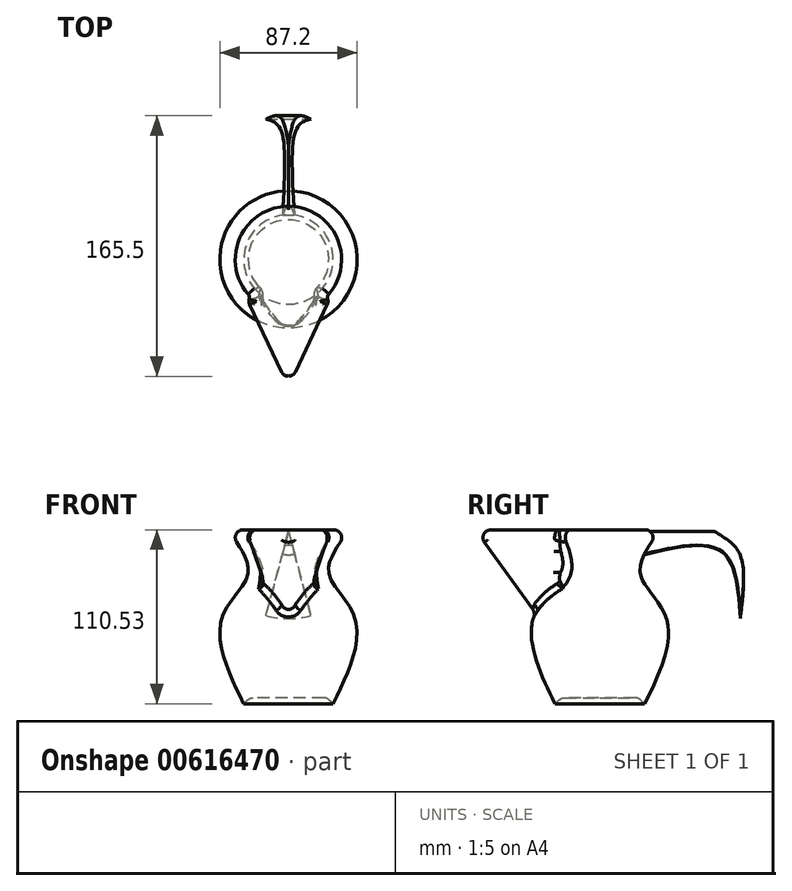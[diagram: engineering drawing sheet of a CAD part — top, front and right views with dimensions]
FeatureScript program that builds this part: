
annotation { "Feature Type Name" : "Feature", "Feature Type Description" : "" }
export const myFeature = defineFeature(function(context is Context, id is Id, definition is map)
    precondition{}
    {
        {
            var Q0;
            Q0=qCreatedBy(makeId("Front.planeOp"),FACE);
            var sketch = newSketch(context, id + "F0", { "sketchPlane" : qUnion([Q0])});
            skLineSegment(sketch, "E0", {"start": v(0, 56.43) * mm, "end": v(0, -56.06) * mm});
            skLineSegment(sketch, "E1", {"start": v(0, 56.43) * mm, "end": v(-38.4, 56.43) * mm});
            skFitSpline(sketch, "E2", {"points": [v(-38.4, 56.43) * mm, v(-26.17, 26.6) * mm, v(-42.35, 0) * mm, v(-27.43, -55.98) * mm], "startDerivative": vector(98.97, -136.85) * mm, "endDerivative": vector(82.52, -160.43) * mm});
            skLineSegment(sketch, "E3", {"start": v(0, -56.06) * mm, "end": v(-27.43, -55.98) * mm});
            skSolve(sketch);
        }
        {
            var Q0;
            Q0=makeQuery(id+"F0.imprint","IMPRINT",FACE,{"disambiguationData":[TD([[makeQuery(id+"F0.imprint","IMPRINT",EDGE,{"derivedFrom":sQuery(id+"F0.wireOp",EDGE,"E0")}),-1.0]])]});
            var Q1;
            Q1=sQuery(id+"F0.wireOp",EDGE,"E0");
            revolve(context, id + "F1", {"entities" : qUnion([Q0]), "axis" : qUnion([Q1]), "revolveType" : RevolveType.FULL});
        }
        {
            var Q0;
            Q0=qCreatedBy(makeId("Top.planeOp"),FACE);
            var sketch = newSketch(context, id + "F2", { "sketchPlane" : qUnion([Q0])});
            skCircle(sketch, "E4", {"center": v(0, 0) * mm, "radius": 22.62 * mm});
            skSolve(sketch);
        }
        {
            var Q0;
            Q0 = qSketchRegion(id + "F2", true);
            extrude(context, id + "F3", {"entities" : qUnion([Q0]), "operationType" : NewBodyOperationType.REMOVE, "oppositeDirection" : true, "depth" : 117.86 * mm, "offsetDistance" : 25.4 * mm, "hasDraft" : true, "draftAngle" : 3 * degree, "hasSecondDirection" : true, "secondDirectionOppositeDirection" : true, "secondDirectionDepth" : 50.3 * mm});
        }
        {
            var Q0;
            Q0=makeQuery(id+"F3.boolean.opBoolean","INTERSECT",EDGE,{"derivedFrom":[makeQuery(id+"F1.opRevolve","SWEPT_FACE",FACE,{"disambiguationData":[OSD([sQuery(id+"F0.wireOp",EDGE,"E3")])]}),makeQuery(id+"F3.opExtrude","SWEPT_FACE",FACE,{"disambiguationData":[OSD([sQuery(id+"F2.wireOp",EDGE,"E4")])]})]});
            chamfer(context, id + "F4", {"entities" : qUnion([Q0]), "width" : 5.08 * mm, "tangentPropagation" : true});
        }
        {
            var Q0;
            Q0=makeQuery(id+"F3.boolean.opBoolean","COPY",FACE,{"derivedFrom":makeQuery(id+"F3.opExtrude","CAP_FACE",FACE,{"disambiguationData":[OSD([sQuery(id+"F2.wireOp",EDGE,"E4")])],"isStart":true})});
            fillet(context, id + "F5", {"entities" : qUnion([Q0]), "radius" : 5.08 * mm, "tangentPropagation" : true, "allowEdgeOverflow" : false});
        }
        {
            var Q0;
            Q0=makeQuery(id+"F3.boolean.opBoolean","COPY",FACE,{"derivedFrom":makeQuery(id+"F3.opExtrude","CAP_FACE",FACE,{"disambiguationData":[OSD([sQuery(id+"F2.wireOp",EDGE,"E4")])],"isStart":true})});
            var Q1;
            {var subQ0=sQuery(id+"F2.wireOp",EDGE,"E4");Q1=makeQuery(id+"F5.opFillet","BLEND_EDGE",EDGE,{"blendedFrom":[makeQuery(id+"F3.boolean.opBoolean","COPY",EDGE,{"derivedFrom":makeQuery(id+"F3.opExtrude","CAP_EDGE",EDGE,{"disambiguationData":[OSD([subQ0])],"isStart":true})}),makeQuery(id+"F4.opChamfer","BLEND_FACE",FACE,{"disambiguationData":[OSD([sQuery(id+"F0.wireOp",EDGE,"E3"),subQ0])]})],"blendedInto":[makeQuery(id+"F4.opChamfer","BLEND_FACE",FACE,{"disambiguationData":[OSD([sQuery(id+"F0.wireOp",EDGE,"E3"),subQ0])]})]});}
            fillet(context, id + "F6", {"entities" : qUnion([Q0, Q1]), "radius" : 5.08 * mm, "tangentPropagation" : true, "allowEdgeOverflow" : false});
        }
        {
            var Q0;
            Q0=qCreatedBy(makeId("Right.planeOp"),FACE);
            var sketch = newSketch(context, id + "F7", { "sketchPlane" : qUnion([Q0])});
            skLineSegment(sketch, "E5", {"start": v(37.1, 55.5) * mm, "end": v(72.6, 55.5) * mm});
            skFitSpline(sketch, "E6", {"points": [v(72.6, 55.5) * mm, v(88.74, 40.47) * mm, v(89.12, 0) * mm], "startDerivative": vector(45.97, -27.95) * mm, "endDerivative": vector(-10.1, -80.42) * mm});
            skFitSpline(sketch, "E7", {"points": [v(89.12, 0) * mm, v(77.1, 42.54) * mm, v(22.63, 39.16) * mm], "startDerivative": vector(-6.87, 112.6) * mm, "endDerivative": vector(-124.04, -31.75) * mm});
            skLineSegment(sketch, "E8", {"start": v(22.63, 39.16) * mm, "end": v(22.63, 41.41) * mm});
            skLineSegment(sketch, "E9", {"start": v(22.63, 41.41) * mm, "end": v(28.45, 47.99) * mm});
            skLineSegment(sketch, "E10", {"start": v(28.45, 47.99) * mm, "end": v(33.9, 53.43) * mm});
            skLineSegment(sketch, "E11", {"start": v(33.9, 53.43) * mm, "end": v(37.1, 55.5) * mm});
            skSolve(sketch);
        }
        {
            var Q0;
            Q0=makeQuery(id+"F7.imprint","IMPRINT",FACE,{"disambiguationData":[TD([[makeQuery(id+"F7.imprint","IMPRINT",EDGE,{"derivedFrom":sQuery(id+"F7.wireOp",EDGE,"E5")}),-1.0]])]});
            var Q1;
            Q1=sQuery(id+"F7.wireOp",EDGE,"E5");
            revolve(context, id + "F8", {"operationType" : NewBodyOperationType.ADD, "entities" : qUnion([Q0]), "axis" : qUnion([Q1]), "revolveType" : RevolveType.SYMMETRIC, "angle" : 30 * degree});
        }
        {
            var Q0;
            Q0=makeQuery(id+"F1.opRevolve","SWEPT_FACE",FACE,{"disambiguationData":[OSD([sQuery(id+"F0.wireOp",EDGE,"E1")])]});
            var sketch = newSketch(context, id + "F9", { "sketchPlane" : qUnion([Q0])});
            skLineSegment(sketch, "E12", {"start": v(0, 0) * mm, "end": v(0, -85.04) * mm, "construction": true});
            skLineSegment(sketch, "E13", {"start": v(0, 22.04) * mm, "end": v(27.45, -26.86) * mm});
            skLineSegment(sketch, "E14", {"start": v(27.45, -26.86) * mm, "end": v(0, -85.04) * mm});
            skLineSegment(sketch, "E15.MirrorCS", {"start": v(-27.45, -26.86) * mm, "end": v(0, -85.04) * mm});
            skLineSegment(sketch, "E16.MirrorCS", {"start": v(0, 22.04) * mm, "end": v(-27.45, -26.86) * mm});
            skSolve(sketch);
        }
        {
            var Q0;
            {var subQ0=sQuery(id+"F9.wireOp",EDGE,"E14");Q0=makeQuery(id+"F9.imprint","IMPRINT",FACE,{"disambiguationData":[TD([[makeQuery(id+"F9.imprint","IMPRINT",EDGE,{"derivedFrom":subQ0}),-1.0]])]});}
            var Q1;
            {var subQ0=sQuery(id+"F9.wireOp",EDGE,"E13");Q1=makeQuery(id+"F9.imprint","IMPRINT",FACE,{"disambiguationData":[TD([[makeQuery(id+"F9.imprint","IMPRINT",EDGE,{"derivedFrom":subQ0}),-1.0]])]});}
            extrude(context, id + "F10", {"entities" : qUnion([Q0, Q1]), "operationType" : NewBodyOperationType.ADD, "oppositeDirection" : true, "depth" : 60.45 * mm, "offsetDistance" : 25.4 * mm, "hasDraft" : true, "draftAngle" : 17 * degree, "draftPullDirection" : true});
        }
        {
            var Q0;
            Q0=makeQuery(id+"F10.boolean.opBoolean","INTERSECT",EDGE,{"derivedFrom":[makeQuery(id+"F1.opRevolve","SWEPT_FACE",FACE,{"disambiguationData":[OSD([sQuery(id+"F0.wireOp",EDGE,"E2")])]}),makeQuery(id+"F10.opExtrude","SWEPT_FACE",FACE,{"disambiguationData":[OSD([sQuery(id+"F9.wireOp",EDGE,"E13")])]})]});
            var Q1;
            Q1=makeQuery(id+"F10.boolean.opBoolean","INTERSECT",EDGE,{"derivedFrom":[makeQuery(id+"F1.opRevolve","SWEPT_FACE",FACE,{"disambiguationData":[OSD([sQuery(id+"F0.wireOp",EDGE,"E2")])]}),makeQuery(id+"F10.opExtrude","SWEPT_FACE",FACE,{"disambiguationData":[OSD([sQuery(id+"F9.wireOp",EDGE,"E14")])]})]});
            var Q2;
            Q2=makeQuery(id+"F10.boolean.opBoolean","INTERSECT",EDGE,{"derivedFrom":[makeQuery(id+"F1.opRevolve","SWEPT_FACE",FACE,{"disambiguationData":[OSD([sQuery(id+"F0.wireOp",EDGE,"E2")])]}),makeQuery(id+"F10.opExtrude","SWEPT_FACE",FACE,{"disambiguationData":[OSD([sQuery(id+"F9.wireOp",EDGE,"E15.MirrorCS")])]})]});
            var Q3;
            Q3=makeQuery(id+"F10.boolean.opBoolean","INTERSECT",EDGE,{"derivedFrom":[makeQuery(id+"F1.opRevolve","SWEPT_FACE",FACE,{"disambiguationData":[OSD([sQuery(id+"F0.wireOp",EDGE,"E2")])]}),makeQuery(id+"F10.opExtrude","SWEPT_FACE",FACE,{"disambiguationData":[OSD([sQuery(id+"F9.wireOp",EDGE,"E16.MirrorCS")])]})]});
            var Q4;
            Q4=makeQuery(id+"F10.opExtrude","CAP_EDGE",EDGE,{"disambiguationData":[OSD([sQuery(id+"F9.wireOp",EDGE,"E15.MirrorCS")])],"isStart":true});
            var Q5;
            Q5=makeQuery(id+"F10.opExtrude","CAP_EDGE",EDGE,{"disambiguationData":[OSD([sQuery(id+"F9.wireOp",EDGE,"E14")])],"isStart":true});
            var Q6;
            Q6=makeQuery(id+"F10.opExtrude","SWEPT_EDGE",EDGE,{"disambiguationData":[OSD([sQuery(id+"F9.wireOp",EDGE,"E14"),sQuery(id+"F9.wireOp",EDGE,"E15.MirrorCS")])]});
            fillet(context, id + "F11", {"entities" : qUnion([Q0, Q1, Q2, Q3, Q4, Q5, Q6]), "radius" : 5 * mm, "tangentPropagation" : true, "allowEdgeOverflow" : false});
        }
        {
            var Q0;
            Q0=makeQuery(id+"F10.opExtrude","SWEPT_EDGE",EDGE,{"disambiguationData":[OSD([sQuery(id+"F0.wireOp",EDGE,"E1"),sQuery(id+"F0.wireOp",EDGE,"E2"),sQuery(id+"F9.wireOp",EDGE,"E13"),sQuery(id+"F9.wireOp",EDGE,"E14")])]});
            var Q1;
            Q1=makeQuery(id+"F10.opExtrude","SWEPT_EDGE",EDGE,{"disambiguationData":[OSD([sQuery(id+"F0.wireOp",EDGE,"E1"),sQuery(id+"F0.wireOp",EDGE,"E2"),sQuery(id+"F9.wireOp",EDGE,"E15.MirrorCS"),sQuery(id+"F9.wireOp",EDGE,"E16.MirrorCS")])]});
            fillet(context, id + "F12", {"entities" : qUnion([Q0, Q1]), "radius" : 5 * mm, "tangentPropagation" : true, "allowEdgeOverflow" : false});
        }
    });
